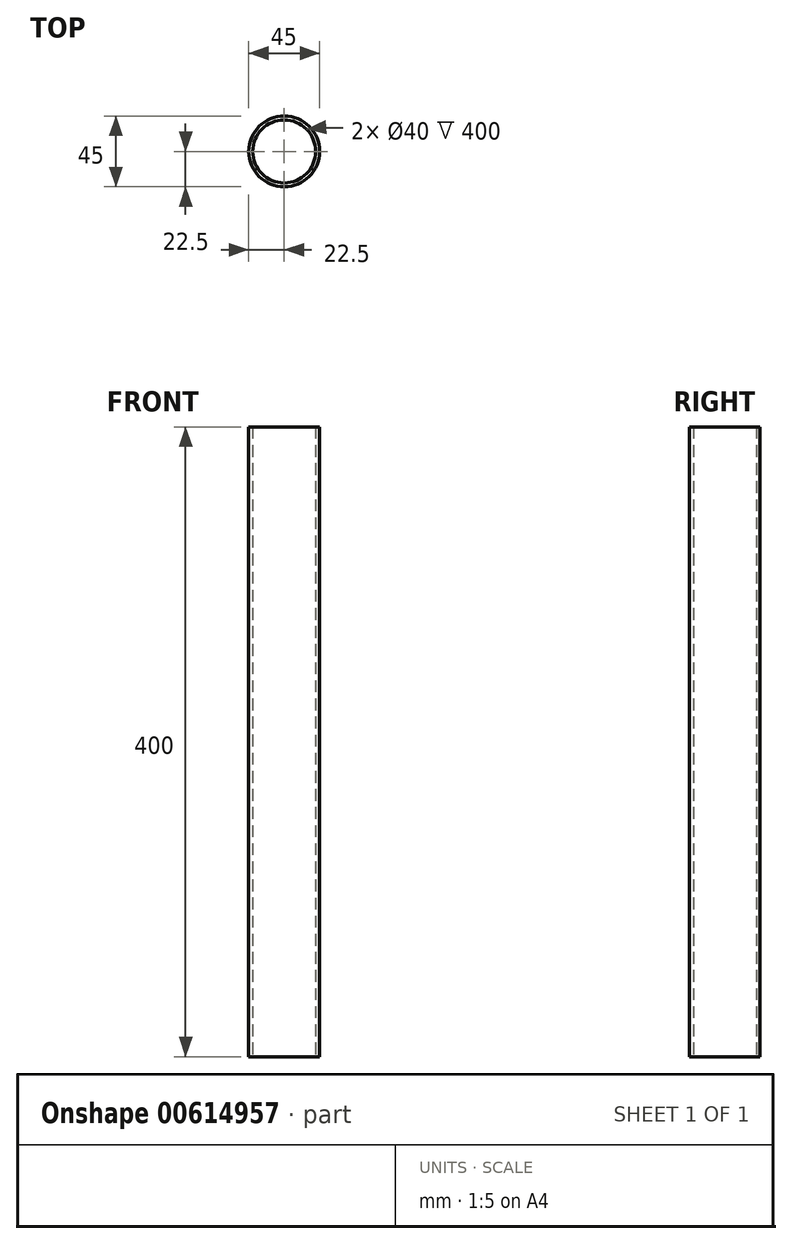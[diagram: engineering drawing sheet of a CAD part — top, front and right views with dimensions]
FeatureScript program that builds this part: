
annotation { "Feature Type Name" : "Feature", "Feature Type Description" : "" }
export const myFeature = defineFeature(function(context is Context, id is Id, definition is map)
    precondition{}
    {
        {
            var Q0;
            Q0=qCreatedBy(makeId("Top.planeOp"),FACE);
            var sketch = newSketch(context, id + "F0", { "sketchPlane" : qUnion([Q0])});
            skCircle(sketch, "E0", {"center": v(0, 0) * mm, "radius": 22.5 * mm});
            skCircle(sketch, "E1", {"center": v(0, 0) * mm, "radius": 20 * mm});
            skSolve(sketch);
        }
        {
            var Q0;
            Q0=makeQuery(id+"F0.imprint","IMPRINT",FACE,{"disambiguationData":[TD([[makeQuery(id+"F0.imprint","IMPRINT",EDGE,{"derivedFrom":sQuery(id+"F0.wireOp",EDGE,"E0")}),1.0]])]});
            var Q1;
            Q1 = qSketchRegion(id + "F0", true);
            extrude(context, id + "F1", {"entities" : qUnion([Q0, Q1]), "depth" : 400 * mm, "offsetDistance" : 25 * mm});
        }
    });
